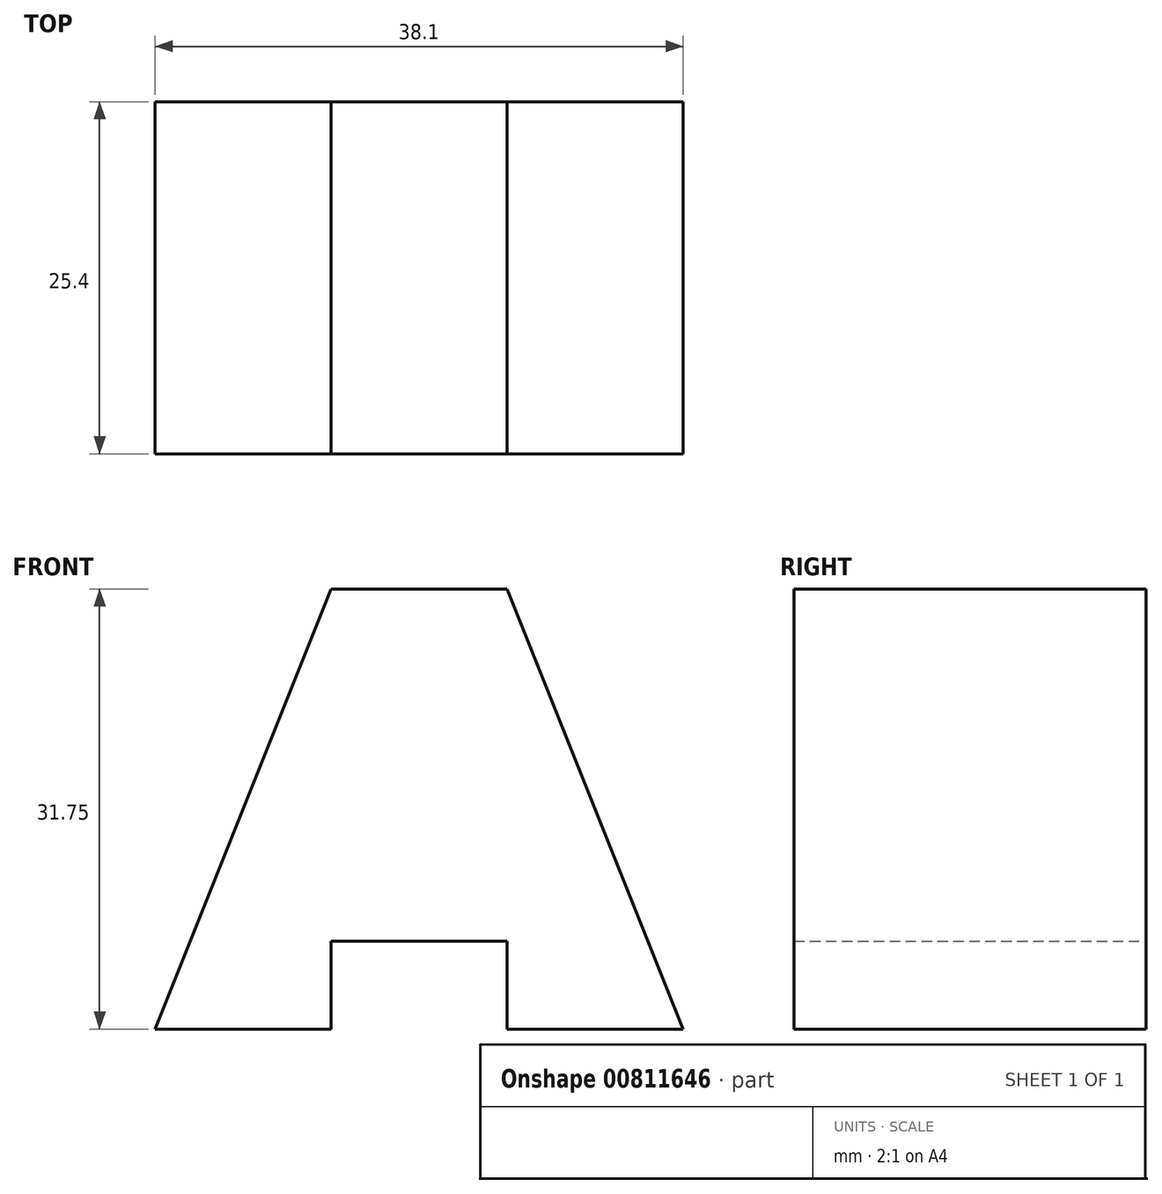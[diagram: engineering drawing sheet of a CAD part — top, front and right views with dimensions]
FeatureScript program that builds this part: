
annotation { "Feature Type Name" : "Feature", "Feature Type Description" : "" }
export const myFeature = defineFeature(function(context is Context, id is Id, definition is map)
    precondition{}
    {
        {
            var Q0;
            Q0=qCreatedBy(makeId("Front.planeOp"),FACE);
            var sketch = newSketch(context, id + "F0", { "sketchPlane" : qUnion([Q0])});
            skLineSegment(sketch, "E0", {"start": v(0, 0) * mm, "end": v(12.7, 0) * mm});
            skLineSegment(sketch, "E1", {"start": v(12.7, 0) * mm, "end": v(12.7, 6.35) * mm});
            skLineSegment(sketch, "E2", {"start": v(12.7, 6.35) * mm, "end": v(25.4, 6.35) * mm});
            skLineSegment(sketch, "E3", {"start": v(25.4, 6.35) * mm, "end": v(25.4, 0) * mm});
            skLineSegment(sketch, "E4", {"start": v(25.4, 0) * mm, "end": v(38.1, 0) * mm});
            skLineSegment(sketch, "E5", {"start": v(12.7, 31.75) * mm, "end": v(0, 0) * mm});
            skLineSegment(sketch, "E6", {"start": v(12.7, 31.75) * mm, "end": v(25.4, 31.75) * mm});
            skLineSegment(sketch, "E7", {"start": v(25.4, 31.75) * mm, "end": v(38.1, 0) * mm});
            skSolve(sketch);
        }
        {
            var Q0;
            Q0 = qSketchRegion(id + "F0", true);
            extrude(context, id + "F1", {"entities" : qUnion([Q0]), "depth" : 25.4 * mm, "offsetDistance" : 25.4 * mm});
        }
    });
